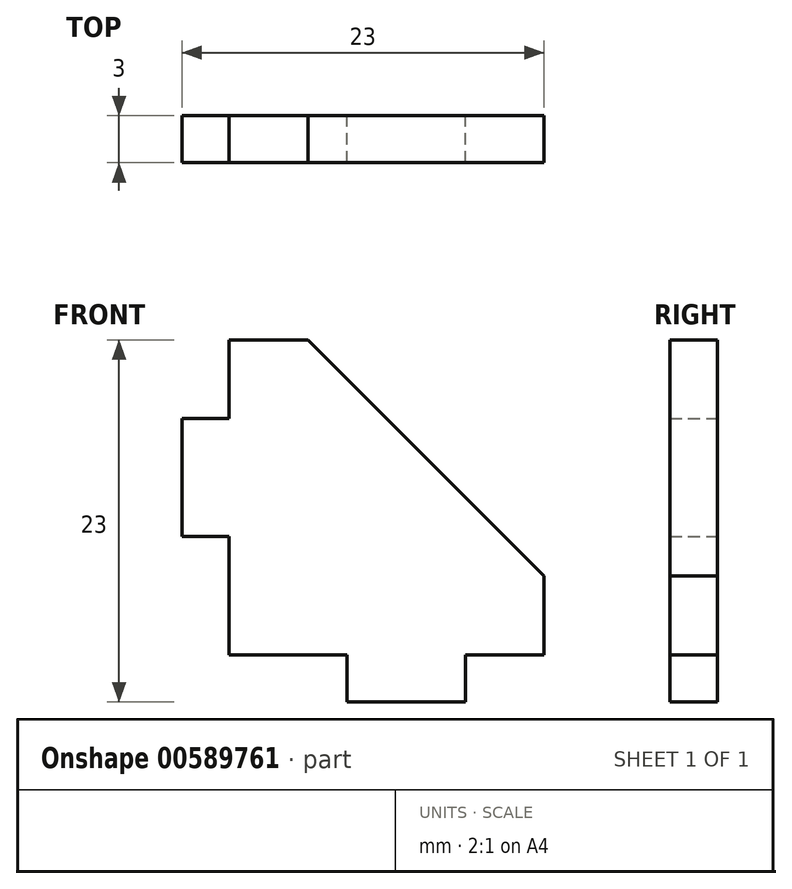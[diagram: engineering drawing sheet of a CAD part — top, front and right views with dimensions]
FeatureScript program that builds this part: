
annotation { "Feature Type Name" : "Feature", "Feature Type Description" : "" }
export const myFeature = defineFeature(function(context is Context, id is Id, definition is map)
    precondition{}
    {
        {
            var Q0;
            Q0=qCreatedBy(makeId("Front.planeOp"),FACE);
            var sketch = newSketch(context, id + "F0", { "sketchPlane" : qUnion([Q0])});
            skLineSegment(sketch, "E0", {"start": v(0, 0) * mm, "end": v(7.5, 0) * mm});
            skLineSegment(sketch, "E1", {"start": v(7.5, 0) * mm, "end": v(7.5, -3) * mm});
            skLineSegment(sketch, "E2", {"start": v(7.5, -3) * mm, "end": v(15, -3) * mm});
            skLineSegment(sketch, "E3", {"start": v(15, -3) * mm, "end": v(15, 0) * mm});
            skLineSegment(sketch, "E4", {"start": v(15, 0) * mm, "end": v(20, 0) * mm});
            skPoint(sketch, "E4.endSnap0", {"position": v(3.75, 0) * mm});
            skLineSegment(sketch, "E5", {"start": v(0, 0) * mm, "end": v(0, 7.5) * mm});
            skLineSegment(sketch, "E6", {"start": v(0, 7.5) * mm, "end": v(-3, 7.5) * mm});
            skLineSegment(sketch, "E7", {"start": v(-3, 7.5) * mm, "end": v(-3, 15) * mm});
            skLineSegment(sketch, "E8", {"start": v(-3, 15) * mm, "end": v(0, 15) * mm});
            skLineSegment(sketch, "E9", {"start": v(0, 15) * mm, "end": v(0, 20) * mm});
            skLineSegment(sketch, "E10", {"start": v(0, 20) * mm, "end": v(5, 20) * mm});
            skLineSegment(sketch, "E11", {"start": v(20, 0) * mm, "end": v(20, 5) * mm});
            skLineSegment(sketch, "E12", {"start": v(20, 5) * mm, "end": v(5, 20) * mm});
            skSolve(sketch);
        }
        {
            var Q0;
            Q0 = qSketchRegion(id + "F0", true);
            extrude(context, id + "F1", {"entities" : qUnion([Q0]), "depth" : 3 * mm, "offsetDistance" : 25 * mm});
        }
    });
